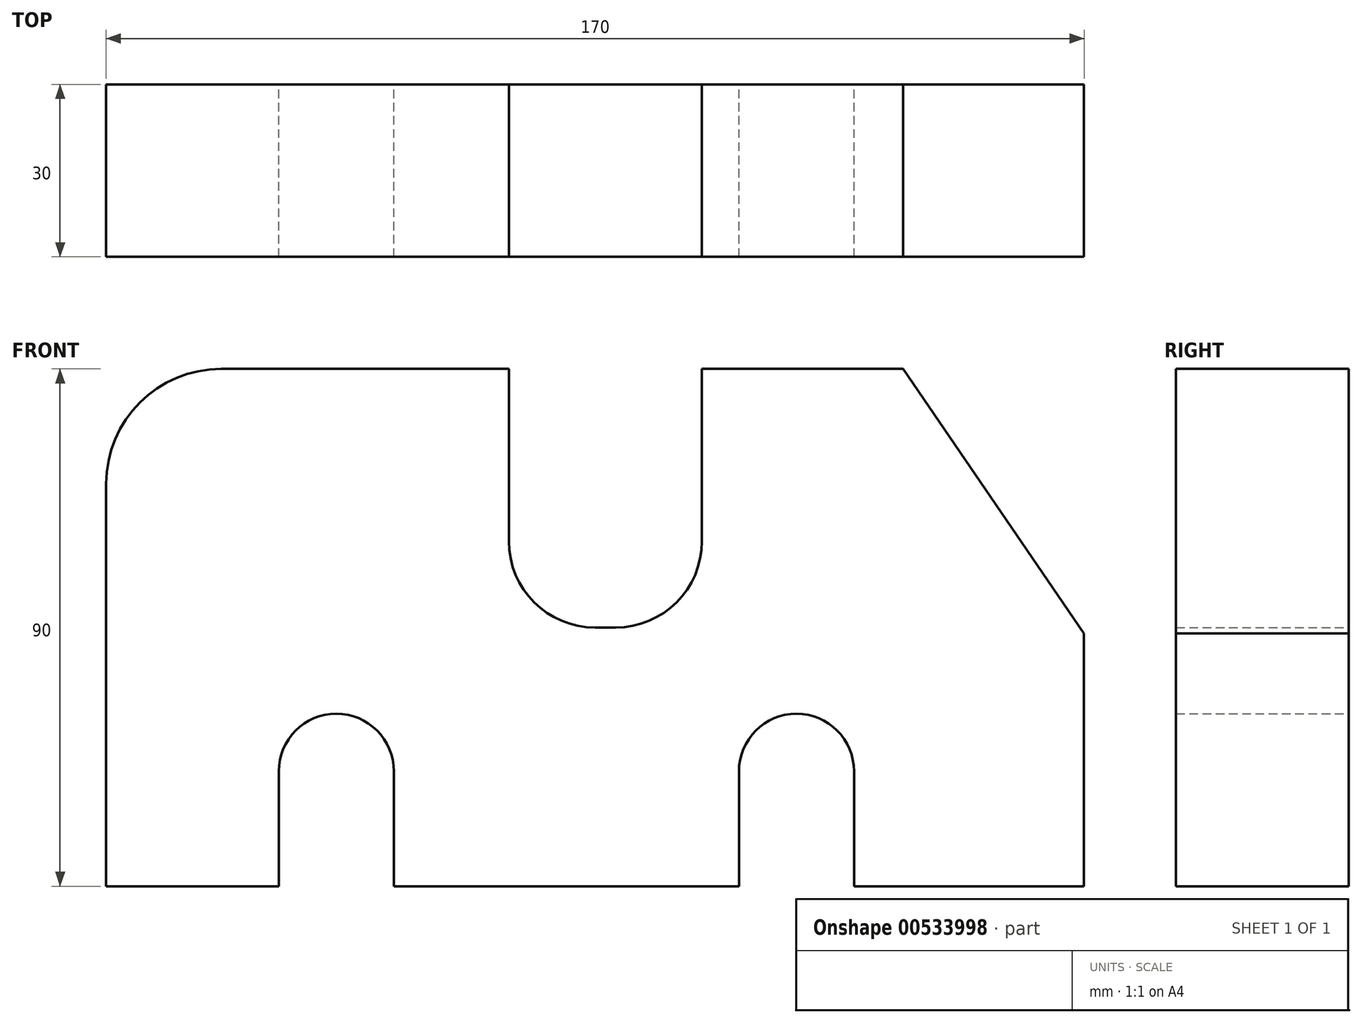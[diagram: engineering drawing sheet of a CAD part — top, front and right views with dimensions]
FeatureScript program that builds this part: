
annotation { "Feature Type Name" : "Feature", "Feature Type Description" : "" }
export const myFeature = defineFeature(function(context is Context, id is Id, definition is map)
    precondition{}
    {
        {
            var Q0;
            Q0=qCreatedBy(makeId("Front.planeOp"),FACE);
            var sketch = newSketch(context, id + "F0", { "sketchPlane" : qUnion([Q0])});
            skLineSegment(sketch, "E0", {"start": v(-82.66, -35) * mm, "end": v(-82.66, 35) * mm});
            skLineSegment(sketch, "E1", {"start": v(-62.66, 55) * mm, "end": v(-12.66, 55) * mm});
            skLineSegment(sketch, "E2", {"start": v(-12.66, 55) * mm, "end": v(-12.66, 25) * mm});
            skLineSegment(sketch, "E3", {"start": v(2.34, 10) * mm, "end": v(5.9, 10) * mm});
            skLineSegment(sketch, "E4", {"start": v(20.9, 25) * mm, "end": v(20.9, 55) * mm});
            skLineSegment(sketch, "E5", {"start": v(20.9, 55) * mm, "end": v(55.9, 55) * mm});
            skLineSegment(sketch, "E6", {"start": v(55.9, 55) * mm, "end": v(87.34, 9) * mm});
            skLineSegment(sketch, "E7", {"start": v(87.34, 9) * mm, "end": v(87.34, -35) * mm});
            skLineSegment(sketch, "E8", {"start": v(87.34, -35) * mm, "end": v(47.34, -35) * mm});
            skLineSegment(sketch, "E9", {"start": v(47.34, -35) * mm, "end": v(47.34, -15) * mm});
            skLineSegment(sketch, "E10", {"start": v(37.34, -5) * mm, "end": v(37.34, -5) * mm});
            skLineSegment(sketch, "E11", {"start": v(27.34, -15) * mm, "end": v(27.34, -35) * mm});
            skLineSegment(sketch, "E12", {"start": v(27.34, -35) * mm, "end": v(-32.66, -35) * mm});
            skLineSegment(sketch, "E13", {"start": v(-32.66, -35) * mm, "end": v(-32.66, -15) * mm});
            skLineSegment(sketch, "E14", {"start": v(-42.66, -5) * mm, "end": v(-42.66, -5) * mm});
            skLineSegment(sketch, "E15", {"start": v(-52.66, -15) * mm, "end": v(-52.66, -35) * mm});
            skLineSegment(sketch, "E16", {"start": v(-52.66, -35) * mm, "end": v(-82.66, -35) * mm});
            skPoint(sketch, "E17.visualSharp", {"position": v(-82.66, 55) * mm});
            skArc(sketch, "E17.filletArc", {"start": v(-62.66, 55) * mm, "mid": v(-76.8, 49.13) * mm, "end": v(-82.66, 35) * mm});
            skPoint(sketch, "E18.visualSharp", {"position": v(-12.66, 10) * mm});
            skArc(sketch, "E18.filletArc", {"start": v(-12.66, 25) * mm, "mid": v(-8.27, 14.38) * mm, "end": v(2.34, 10) * mm});
            skPoint(sketch, "E19.visualSharp", {"position": v(20.9, 10) * mm});
            skArc(sketch, "E19.filletArc", {"start": v(5.9, 10) * mm, "mid": v(16.5, 14.38) * mm, "end": v(20.9, 25) * mm});
            skPoint(sketch, "E20.visualSharp", {"position": v(-52.66, -5) * mm});
            skArc(sketch, "E20.filletArc", {"start": v(-42.66, -5) * mm, "mid": v(-49.73, -7.94) * mm, "end": v(-52.66, -15) * mm});
            skPoint(sketch, "E21.visualSharp", {"position": v(27.34, -5) * mm});
            skArc(sketch, "E21.filletArc", {"start": v(37.34, -5) * mm, "mid": v(30.27, -7.94) * mm, "end": v(27.34, -15) * mm});
            skPoint(sketch, "E22.visualSharp", {"position": v(47.34, -5) * mm});
            skArc(sketch, "E22.filletArc", {"start": v(47.34, -15) * mm, "mid": v(44.41, -7.94) * mm, "end": v(37.34, -5) * mm});
            skPoint(sketch, "E23.visualSharp", {"position": v(-32.66, -5) * mm});
            skArc(sketch, "E23.filletArc", {"start": v(-32.66, -15) * mm, "mid": v(-35.59, -7.94) * mm, "end": v(-42.66, -5) * mm});
            skSolve(sketch);
        }
        {
            var Q0;
            Q0 = qSketchRegion(id + "F0", true);
            extrude(context, id + "F1", {"entities" : qUnion([Q0]), "depth" : 30 * mm, "offsetDistance" : 25 * mm});
        }
    });
